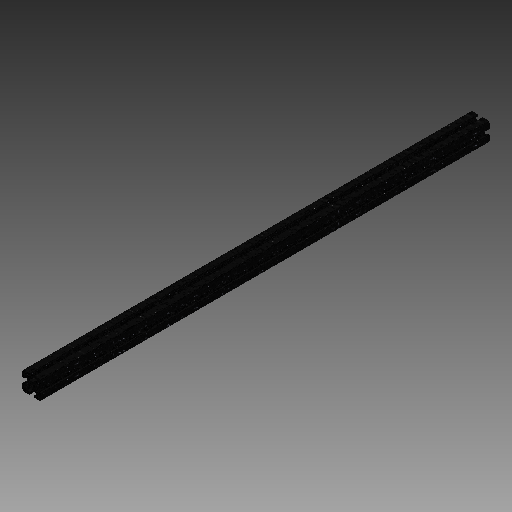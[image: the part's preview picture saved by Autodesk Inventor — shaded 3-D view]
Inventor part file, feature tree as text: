
AUTODESK INVENTOR PART (.ipt)
format: ipt  version: 2019 (Build 230136000, 136)  size: 248,320 bytes
history: native  units: in
note: dims shown in document units (in); Inventor stores cm internally (conversion verified against a paired STEP export)
features: plane x1, extrude x1, sketch x1
ambient origin geometry x8: Origin, YZ Plane, XZ Plane, XY Plane, X Axis, Y Axis, Z Axis, Center Point
bodies: Solid1 (feature_tree)
feature tree (3):
  plane  "Work Plane1"
  extrude  "Extrusion1"  [1 undecoded]
  sketch  "Sketch1"  dims[d0=36.0in d1=0.0in]
note: 1 required parameter value undecoded (feature->parameter linkage not recoverable at this tier; creation-order binding heuristic only, values carry confidence <= 0.55)
